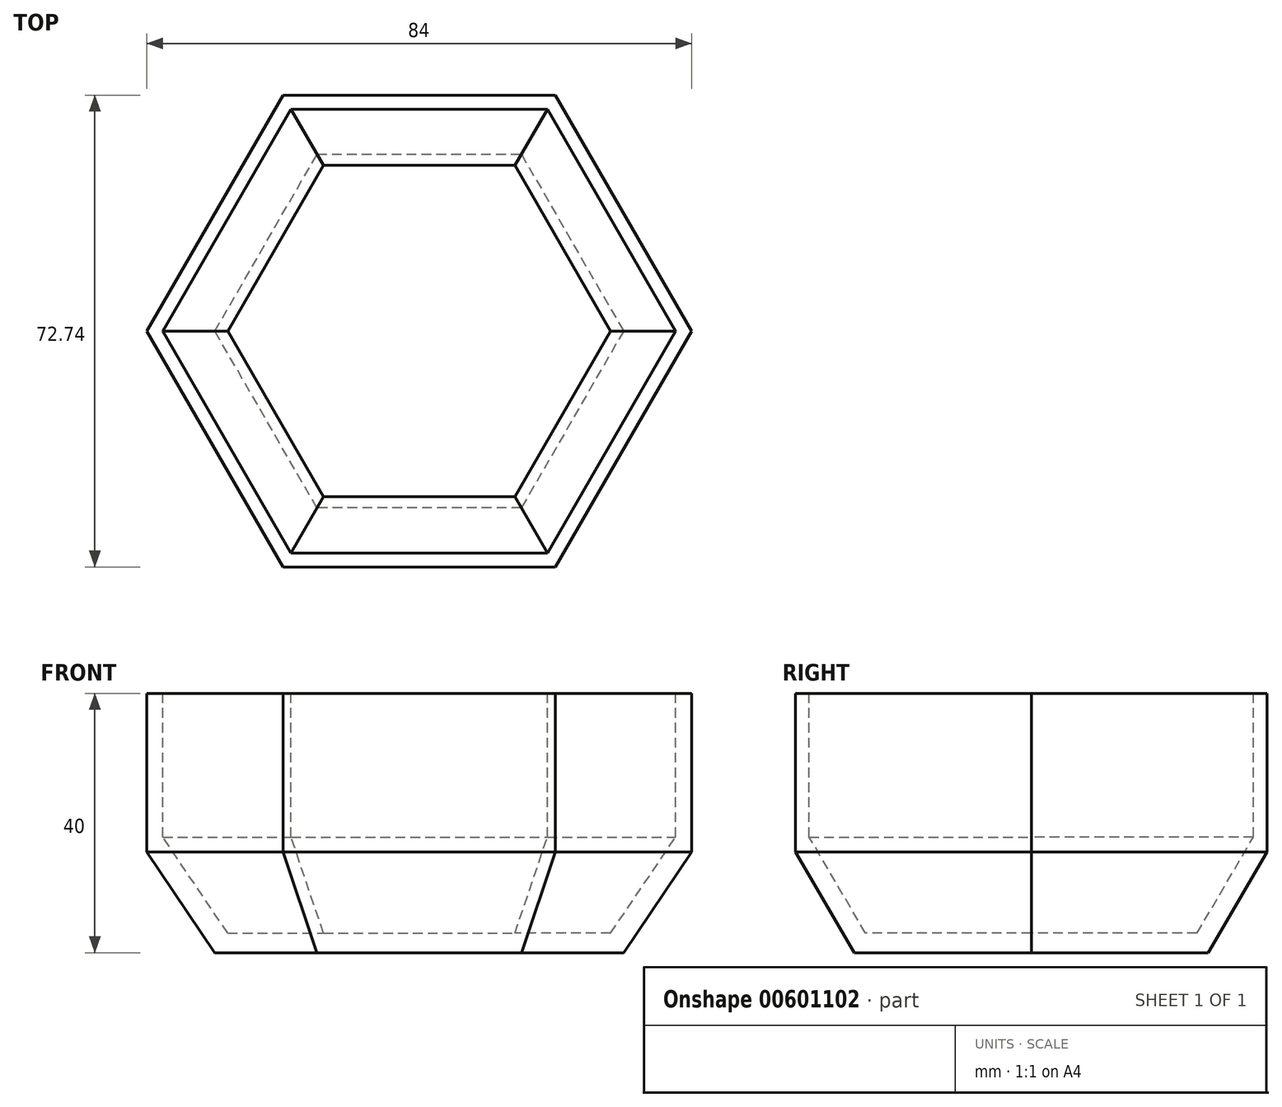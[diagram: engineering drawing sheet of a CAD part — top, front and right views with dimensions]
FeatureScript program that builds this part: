
annotation { "Feature Type Name" : "Feature", "Feature Type Description" : "" }
export const myFeature = defineFeature(function(context is Context, id is Id, definition is map)
    precondition{}
    {
        {
            var Q0;
            Q0=qCreatedBy(makeId("Top.planeOp"),FACE);
            var sketch = newSketch(context, id + "F0", { "sketchPlane" : qUnion([Q0])});
            skCircle(sketch, "E0.cCircle", {"center": v(0, 0) * mm, "radius": 31.5 * mm, "construction": true});
            skLineSegment(sketch, "E0.0", {"start": v(31.5, 0) * mm, "end": v(15.75, -27.28) * mm});
            skLineSegment(sketch, "E0.1", {"start": v(15.75, -27.28) * mm, "end": v(-15.75, -27.28) * mm});
            skLineSegment(sketch, "E0.2", {"start": v(-15.75, -27.28) * mm, "end": v(-31.5, 0) * mm});
            skLineSegment(sketch, "E0.3", {"start": v(-31.5, 0) * mm, "end": v(-15.75, 27.28) * mm});
            skLineSegment(sketch, "E0.4", {"start": v(-15.75, 27.28) * mm, "end": v(15.75, 27.28) * mm});
            skLineSegment(sketch, "E0.5", {"start": v(15.75, 27.28) * mm, "end": v(31.5, 0) * mm});
            skSolve(sketch);
        }
        {
            var Q0;
            Q0=makeQuery(id+"F0.imprint","IMPRINT",FACE,{"disambiguationData":[TD([[makeQuery(id+"F0.imprint","IMPRINT",EDGE,{"derivedFrom":sQuery(id+"F0.wireOp",EDGE,"E0.0")}),-1.0]])]});
            cPlane(context, id + "F1", {"entities" : qUnion([Q0]), "cplaneType" : CPlaneType.OFFSET, "offset" : 20 * mm, "width" : 150 * mm, "height" : 150 * mm});
        }
        {
            var Q0;
            Q0=qCreatedBy(id+"F1.planeOp",FACE);
            var sketch = newSketch(context, id + "F2", { "sketchPlane" : qUnion([Q0])});
            skCircle(sketch, "E1.cCircle", {"center": v(0, 0) * mm, "radius": 45 * mm, "construction": true});
            skLineSegment(sketch, "E1.0", {"start": v(45, 0) * mm, "end": v(22.5, -38.97) * mm});
            skLineSegment(sketch, "E1.1", {"start": v(22.5, -38.97) * mm, "end": v(-22.5, -38.97) * mm});
            skLineSegment(sketch, "E1.2", {"start": v(-22.5, -38.97) * mm, "end": v(-45, 0) * mm});
            skLineSegment(sketch, "E1.3", {"start": v(-45, 0) * mm, "end": v(-22.5, 38.97) * mm});
            skLineSegment(sketch, "E1.4", {"start": v(-22.5, 38.97) * mm, "end": v(22.5, 38.97) * mm});
            skLineSegment(sketch, "E1.5", {"start": v(22.5, 38.97) * mm, "end": v(45, 0) * mm});
            skSolve(sketch);
        }
        {
            var Q0;
            Q0=makeQuery(id+"F0.imprint","IMPRINT",FACE,{"disambiguationData":[TD([[makeQuery(id+"F0.imprint","IMPRINT",EDGE,{"derivedFrom":sQuery(id+"F0.wireOp",EDGE,"E0.0")}),-1.0]])]});
            var Q1;
            Q1=makeQuery(id+"F2.imprint","IMPRINT",FACE,{"disambiguationData":[TD([[makeQuery(id+"F2.imprint","IMPRINT",EDGE,{"derivedFrom":sQuery(id+"F2.wireOp",EDGE,"E1.0")}),-1.0]])]});
            loft(context, id + "F3", {"sheetProfilesArray" : [{ "sheetProfileEntities" : qUnion([Q0]) }, { "sheetProfileEntities" : qUnion([Q1]) }]});
        }
        {
            var Q0;
            Q0=makeQuery(id+"F3.opLoft","CAP_FACE",FACE,{"disambiguationData":[OSD([makeQuery(id+"F2.imprint","IMPRINT",FACE,{"disambiguationData":[TD([[makeQuery(id+"F2.imprint","IMPRINT",EDGE,{"derivedFrom":sQuery(id+"F2.wireOp",EDGE,"E1.0")}),-1.0]])]})])],"isStart":true});
            shell(context, id + "F4", {"entities" : qUnion([Q0]), "thickness" : 3 * mm});
        }
        {
            var Q0;
            Q0=qCreatedBy(id+"F1.planeOp",FACE);
            var sketch = newSketch(context, id + "F5", { "sketchPlane" : qUnion([Q0])});
            skCircle(sketch, "E2.cCircle", {"center": v(0, 0) * mm, "radius": 43 * mm, "construction": true});
            skLineSegment(sketch, "E2.0", {"start": v(43, 0) * mm, "end": v(21.5, -37.24) * mm});
            skLineSegment(sketch, "E2.1", {"start": v(21.5, -37.24) * mm, "end": v(-21.5, -37.24) * mm});
            skLineSegment(sketch, "E2.2", {"start": v(-21.5, -37.24) * mm, "end": v(-43, 0) * mm});
            skLineSegment(sketch, "E2.3", {"start": v(-43, 0) * mm, "end": v(-21.5, 37.24) * mm});
            skLineSegment(sketch, "E2.4", {"start": v(-21.5, 37.24) * mm, "end": v(21.5, 37.24) * mm});
            skLineSegment(sketch, "E2.5", {"start": v(21.5, 37.24) * mm, "end": v(43, 0) * mm});
            skLineSegment(sketch, "E3.0", {"start": v(-39.54, 0) * mm, "end": v(-19.77, 34.24) * mm});
            skLineSegment(sketch, "E3.1", {"start": v(19.77, 34.24) * mm, "end": v(39.54, 0) * mm});
            skLineSegment(sketch, "E3.2", {"start": v(39.54, 0) * mm, "end": v(19.77, -34.24) * mm});
            skLineSegment(sketch, "E3.3", {"start": v(-19.77, 34.24) * mm, "end": v(19.77, 34.24) * mm});
            skLineSegment(sketch, "E3.4", {"start": v(19.77, -34.24) * mm, "end": v(-19.77, -34.24) * mm});
            skLineSegment(sketch, "E3.5", {"start": v(-19.77, -34.24) * mm, "end": v(-39.54, 0) * mm});
            skSolve(sketch);
        }
        {
            var Q0;
            Q0=makeQuery(id+"F5.imprint","IMPRINT",FACE,{"disambiguationData":[TD([[makeQuery(id+"F5.imprint","IMPRINT",EDGE,{"derivedFrom":sQuery(id+"F5.wireOp",EDGE,"E2.0")}),-1.0]])]});
            var Q1;
            Q1=makeQuery(id+"F4.opShell","OFFSET_FACE",FACE,{"disambiguationData":[OSD([sQuery(id+"F0.wireOp",EDGE,"E0.1"),sQuery(id+"F0.wireOp",EDGE,"E0.2"),sQuery(id+"F0.wireOp",EDGE,"E0.3"),sQuery(id+"F2.wireOp",EDGE,"E1.1"),sQuery(id+"F2.wireOp",EDGE,"E1.2"),sQuery(id+"F2.wireOp",EDGE,"E1.3")])]});
            extrude(context, id + "F6", {"entities" : qUnion([Q0]), "operationType" : NewBodyOperationType.ADD, "endBound" : BoundingType.UP_TO_NEXT, "oppositeDirection" : true, "depth" : 6.5 * mm, "endBoundEntityFace" : qUnion([Q1]), "offsetDistance" : 25 * mm});
        }
        {
            var Q0;
            Q0=qCreatedBy(id+"F1.planeOp",FACE);
            var sketch = newSketch(context, id + "F7", { "sketchPlane" : qUnion([Q0])});
            skCircle(sketch, "E4.cCircle", {"center": v(0, 0) * mm, "radius": 42 * mm, "construction": true});
            skLineSegment(sketch, "E4.0", {"start": v(42, 0) * mm, "end": v(21, -36.37) * mm});
            skLineSegment(sketch, "E4.1", {"start": v(21, -36.37) * mm, "end": v(-21, -36.37) * mm});
            skLineSegment(sketch, "E4.2", {"start": v(-21, -36.37) * mm, "end": v(-42, 0) * mm});
            skLineSegment(sketch, "E4.3", {"start": v(-42, 0) * mm, "end": v(-21, 36.37) * mm});
            skLineSegment(sketch, "E4.4", {"start": v(-21, 36.37) * mm, "end": v(21, 36.37) * mm});
            skLineSegment(sketch, "E4.5", {"start": v(21, 36.37) * mm, "end": v(42, 0) * mm});
            skLineSegment(sketch, "E5.0", {"start": v(-39.54, 0) * mm, "end": v(-19.77, 34.24) * mm});
            skLineSegment(sketch, "E5.1", {"start": v(19.77, 34.24) * mm, "end": v(39.54, 0) * mm});
            skLineSegment(sketch, "E5.2", {"start": v(39.54, 0) * mm, "end": v(19.77, -34.24) * mm});
            skLineSegment(sketch, "E5.3", {"start": v(-19.77, 34.24) * mm, "end": v(19.77, 34.24) * mm});
            skLineSegment(sketch, "E5.4", {"start": v(19.77, -34.24) * mm, "end": v(-19.77, -34.24) * mm});
            skLineSegment(sketch, "E5.5", {"start": v(-19.77, -34.24) * mm, "end": v(-39.54, 0) * mm});
            skSolve(sketch);
        }
        {
            var Q0;
            Q0 = qSketchRegion(id + "F7", true);
            extrude(context, id + "F8", {"entities" : qUnion([Q0]), "operationType" : NewBodyOperationType.ADD, "depth" : 20 * mm, "offsetDistance" : 25 * mm});
        }
        {
            var Q0;
            Q0=makeQuery(id+"F6.boolean.opBoolean","MERGE",FACE,{"derivedFrom":[makeQuery(id+"F3.opLoft","CAP_FACE",FACE,{"disambiguationData":[OSD([makeQuery(id+"F2.imprint","IMPRINT",FACE,{"disambiguationData":[TD([[makeQuery(id+"F2.imprint","IMPRINT",EDGE,{"derivedFrom":sQuery(id+"F2.wireOp",EDGE,"E1.0")}),-1.0]])]})])],"isStart":true}),makeQuery(id+"F6.opExtrude","CAP_FACE",FACE,{"disambiguationData":[OSD([sQuery(id+"F5.wireOp",EDGE,"E2.0"),sQuery(id+"F5.wireOp",EDGE,"E2.1"),sQuery(id+"F5.wireOp",EDGE,"E2.2"),sQuery(id+"F5.wireOp",EDGE,"E2.3"),sQuery(id+"F5.wireOp",EDGE,"E2.4"),sQuery(id+"F5.wireOp",EDGE,"E2.5"),sQuery(id+"F5.wireOp",EDGE,"E3.0"),sQuery(id+"F5.wireOp",EDGE,"E3.1"),sQuery(id+"F5.wireOp",EDGE,"E3.2"),sQuery(id+"F5.wireOp",EDGE,"E3.3"),sQuery(id+"F5.wireOp",EDGE,"E3.4"),sQuery(id+"F5.wireOp",EDGE,"E3.5")])],"isStart":true})]});
            extrude(context, id + "F9", {"entities" : qUnion([Q0]), "operationType" : NewBodyOperationType.REMOVE, "oppositeDirection" : true, "depth" : 25 * mm, "offsetDistance" : 25 * mm});
        }
    });
